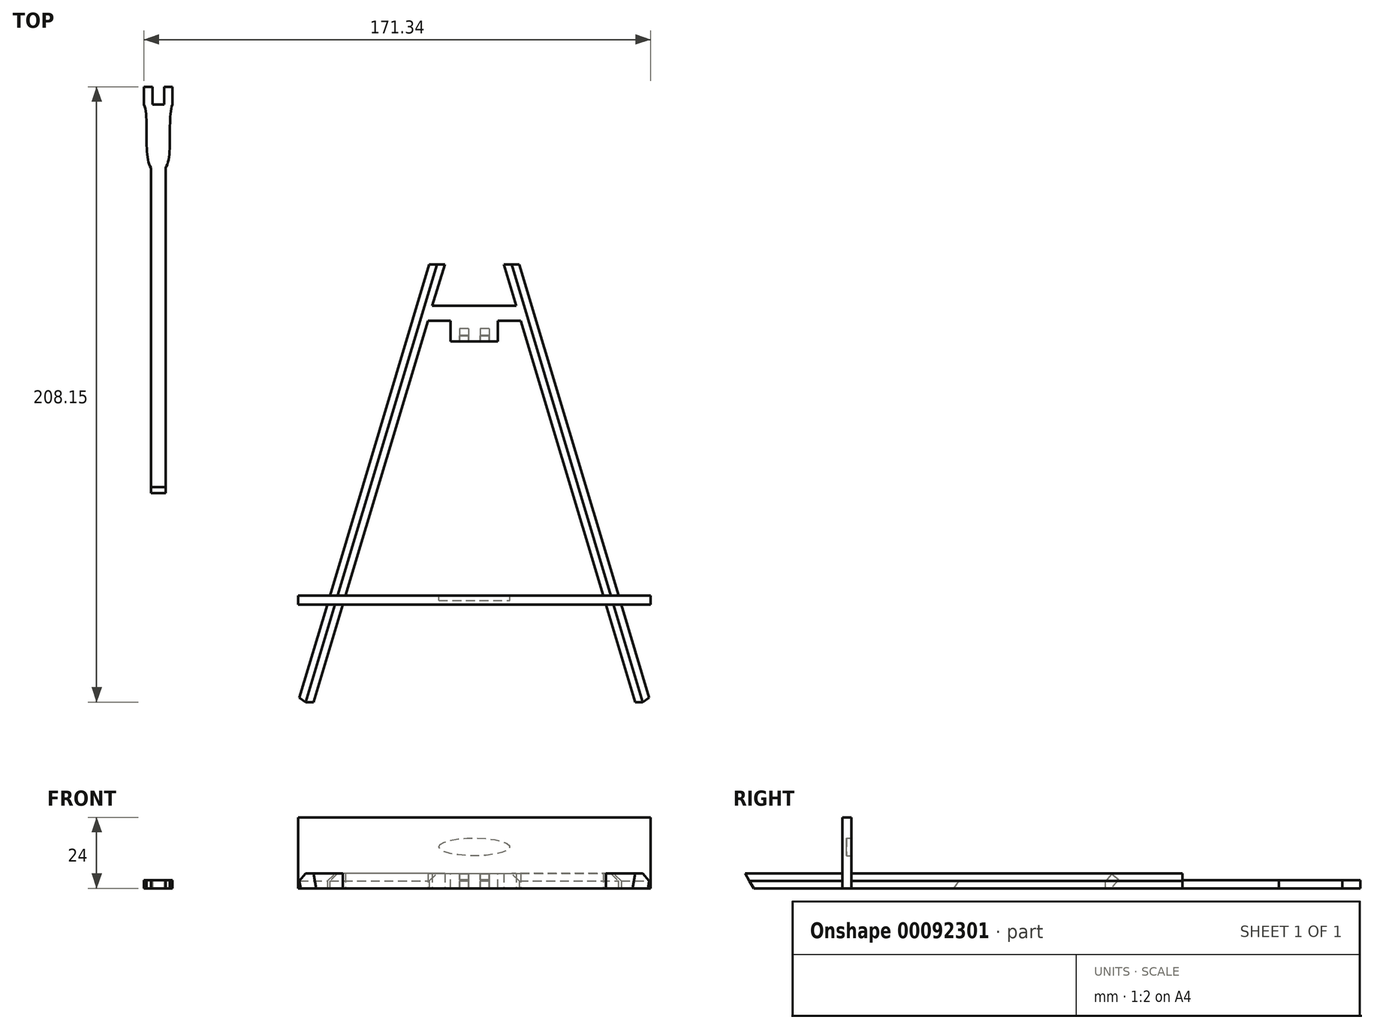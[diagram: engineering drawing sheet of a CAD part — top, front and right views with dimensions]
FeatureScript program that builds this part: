
annotation { "Feature Type Name" : "Feature", "Feature Type Description" : "" }
export const myFeature = defineFeature(function(context is Context, id is Id, definition is map)
    precondition{}
    {
        {
            var Q0;
            Q0=qCreatedBy(makeId("Top.planeOp"),FACE);
            var sketch = newSketch(context, id + "F0", { "sketchPlane" : qUnion([Q0])});
            skLineSegment(sketch, "E0.bottom", {"start": v(-52.21, 78.6) * mm, "end": v(57.79, 78.6) * mm});
            skLineSegment(sketch, "E0.top", {"start": v(-52.21, -71.4) * mm, "end": v(57.79, -71.4) * mm});
            skLineSegment(sketch, "E0.left", {"start": v(-52.21, 78.6) * mm, "end": v(-52.21, -71.4) * mm});
            skLineSegment(sketch, "E0.right", {"start": v(57.79, 78.6) * mm, "end": v(57.79, -71.4) * mm});
            skLineSegment(sketch, "E1", {"start": v(2.79, 78.6) * mm, "end": v(-7.21, 78.6) * mm});
            skLineSegment(sketch, "E2", {"start": v(2.79, 78.6) * mm, "end": v(12.79, 78.6) * mm});
            skLineSegment(sketch, "E3", {"start": v(-7.21, 78.6) * mm, "end": v(-52.21, -71.4) * mm});
            skLineSegment(sketch, "E4", {"start": v(12.79, 78.6) * mm, "end": v(57.79, -71.4) * mm});
            skLineSegment(sketch, "E5", {"start": v(-40.81, -33.4) * mm, "end": v(46.39, -33.4) * mm});
            skLineSegment(sketch, "E6.0", {"start": v(-12, 80.05) * mm, "end": v(-57, -69.95) * mm});
            skLineSegment(sketch, "E7.0", {"start": v(17.58, 80.05) * mm, "end": v(62.58, -69.95) * mm});
            skLineSegment(sketch, "E8.0", {"start": v(-41.71, -36.4) * mm, "end": v(47.29, -36.4) * mm});
            skLineSegment(sketch, "E9", {"start": v(-12, 80.05) * mm, "end": v(-7.21, 78.6) * mm});
            skLineSegment(sketch, "E10", {"start": v(12.79, 78.6) * mm, "end": v(17.58, 80.05) * mm});
            skLineSegment(sketch, "E11", {"start": v(-57, -69.95) * mm, "end": v(-52.21, -71.4) * mm});
            skLineSegment(sketch, "E12", {"start": v(57.79, -71.4) * mm, "end": v(62.58, -69.95) * mm});
            skLineSegment(sketch, "E13", {"start": v(-11.41, 64.6) * mm, "end": v(16.99, 64.6) * mm});
            skLineSegment(sketch, "E14.0", {"start": v(-12.91, 59.6) * mm, "end": v(18.49, 59.6) * mm});
            skLineSegment(sketch, "E15", {"start": v(2.79, 78.6) * mm, "end": v(2.79, 64.6) * mm, "construction": true});
            skLineSegment(sketch, "E16", {"start": v(2.79, -36.4) * mm, "end": v(2.79, -71.4) * mm, "construction": true});
            skSolve(sketch);
        }
        {
            var Q0;
            {var subQ0=sQuery(id+"F0.wireOp",EDGE,"E3");var subQ1=makeQuery(id+"F0.imprint","INTERSECT",VERTEX,{"derivedFrom":[subQ0,sQuery(id+"F0.wireOp",EDGE,"E13")]});Q0=makeQuery(id+"F0.imprint","IMPRINT",FACE,{"disambiguationData":[TD([[makeQuery(id+"F0.imprint","IMPRINT",EDGE,{"disambiguationData":[TD([[subQ1,-1.0]])],"derivedFrom":subQ0}),-1.0]])]});}
            var Q1;
            {var subQ0=sQuery(id+"F0.wireOp",EDGE,"E13");Q1=makeQuery(id+"F0.imprint","IMPRINT",FACE,{"disambiguationData":[TD([[makeQuery(id+"F0.imprint","IMPRINT",EDGE,{"derivedFrom":subQ0}),-1.0]])]});}
            var Q2;
            {var subQ0=sQuery(id+"F0.wireOp",EDGE,"E4");var subQ5=makeQuery(id+"F0.imprint","INTERSECT",VERTEX,{"derivedFrom":[subQ0,sQuery(id+"F0.wireOp",EDGE,"E13")]});Q2=makeQuery(id+"F0.imprint","IMPRINT",FACE,{"disambiguationData":[TD([[makeQuery(id+"F0.imprint","IMPRINT",EDGE,{"disambiguationData":[TD([[subQ5,-1.0]])],"derivedFrom":subQ0}),1.0]])]});}
            var Q3;
            {var subQ0=sQuery(id+"F0.wireOp",EDGE,"E5");Q3=makeQuery(id+"F0.imprint","IMPRINT",FACE,{"disambiguationData":[TD([[makeQuery(id+"F0.imprint","IMPRINT",EDGE,{"derivedFrom":subQ0}),-1.0]])]});}
            var Q4;
            {var subQ0=sQuery(id+"F0.wireOp",EDGE,"E11");Q4=makeQuery(id+"F0.imprint","IMPRINT",FACE,{"disambiguationData":[TD([[makeQuery(id+"F0.imprint","IMPRINT",EDGE,{"derivedFrom":subQ0}),1.0]])]});}
            var Q5;
            {var subQ0=sQuery(id+"F0.wireOp",EDGE,"E12");Q5=makeQuery(id+"F0.imprint","IMPRINT",FACE,{"disambiguationData":[TD([[makeQuery(id+"F0.imprint","IMPRINT",EDGE,{"derivedFrom":subQ0}),1.0]])]});}
            extrude(context, id + "F1", {"entities" : qUnion([Q0, Q1, Q2, Q3, Q4, Q5]), "depth" : 5 * mm});
        }
        {
            var Q0;
            Q0=makeQuery(id+"F1.opExtrude","CAP_FACE",FACE,{"disambiguationData":[OSD([sQuery(id+"F0.wireOp",EDGE,"E0.bottom"),sQuery(id+"F0.wireOp",EDGE,"E3"),sQuery(id+"F0.wireOp",EDGE,"E4"),sQuery(id+"F0.wireOp",EDGE,"E5"),sQuery(id+"F0.wireOp",EDGE,"E6.0"),sQuery(id+"F0.wireOp",EDGE,"E7.0"),sQuery(id+"F0.wireOp",EDGE,"E8.0"),sQuery(id+"F0.wireOp",EDGE,"E11"),sQuery(id+"F0.wireOp",EDGE,"E12"),sQuery(id+"F0.wireOp",EDGE,"E13"),sQuery(id+"F0.wireOp",EDGE,"E14.0")])],"isStart":true});
            var sketch = newSketch(context, id + "F2", { "sketchPlane" : qUnion([Q0])});
            skLineSegment(sketch, "E17.0", {"start": v(-40.81, 33.4) * mm, "end": v(46.39, 33.4) * mm});
            skLineSegment(sketch, "E18.0", {"start": v(-41.71, 36.4) * mm, "end": v(47.29, 36.4) * mm});
            skLineSegment(sketch, "E19", {"start": v(2.79, 3.1) * mm, "end": v(2.79, -57.6) * mm, "construction": true});
            skLineSegment(sketch, "E20", {"start": v(-41.71, 36.4) * mm, "end": v(-56.81, 36.4) * mm});
            skLineSegment(sketch, "E21", {"start": v(-56.81, 33.4) * mm, "end": v(-56.81, 36.4) * mm});
            skLineSegment(sketch, "E22", {"start": v(-56.81, 33.4) * mm, "end": v(-40.81, 33.4) * mm});
            skLineSegment(sketch, "E23.MirrorCS", {"start": v(47.29, 36.4) * mm, "end": v(62.39, 36.4) * mm});
            skLineSegment(sketch, "E24.MirrorCS", {"start": v(62.39, 33.4) * mm, "end": v(62.39, 36.4) * mm});
            skLineSegment(sketch, "E25.MirrorCS", {"start": v(62.39, 33.4) * mm, "end": v(46.39, 33.4) * mm});
            skSolve(sketch);
        }
        {
            var Q0;
            Q0 = qSketchRegion(id + "F2", true);
            extrude(context, id + "F3", {"entities" : qUnion([Q0]), "operationType" : NewBodyOperationType.ADD, "oppositeDirection" : true, "depth" : 24 * mm});
        }
        {
            var Q0;
            Q0=makeQuery(id+"F1.opExtrude","SWEPT_FACE",FACE,{"disambiguationData":[OSD([sQuery(id+"F0.wireOp",EDGE,"E14.0")])]});
            var sketch = newSketch(context, id + "F4", { "sketchPlane" : qUnion([Q0])});
            skLineSegment(sketch, "E26.bottom", {"start": v(10.79, 0) * mm, "end": v(-5.21, 0) * mm});
            skLineSegment(sketch, "E26.top", {"start": v(10.79, 5) * mm, "end": v(-5.21, 5) * mm});
            skLineSegment(sketch, "E26.left", {"start": v(10.79, 0) * mm, "end": v(10.79, 5) * mm});
            skLineSegment(sketch, "E26.right", {"start": v(-5.21, 0) * mm, "end": v(-5.21, 5) * mm});
            skLineSegment(sketch, "E27", {"start": v(2.79, 0) * mm, "end": v(2.79, 5) * mm, "construction": true});
            skSolve(sketch);
        }
        {
            var Q0;
            Q0 = qSketchRegion(id + "F4", true);
            extrude(context, id + "F5", {"entities" : qUnion([Q0]), "operationType" : NewBodyOperationType.ADD, "depth" : 7 * mm});
        }
        {
            var Q0;
            Q0=makeQuery(id+"F5.opExtrude","CAP_EDGE",EDGE,{"disambiguationData":[OSD([sQuery(id+"F4.wireOp",EDGE,"E26.bottom")])],"isStart":false});
            cPlane(context, id + "F6", {"entities" : qUnion([Q0]), "cplaneType" : CPlaneType.LINE_ANGLE, "offset" : 4 * mm, "angle" : 50 * degree, "width" : 150 * mm, "height" : 150 * mm});
        }
        {
            var Q0;
            Q0=qCreatedBy(id+"F6.planeOp",FACE);
            var sketch = newSketch(context, id + "F7", { "sketchPlane" : qUnion([Q0])});
            skLineSegment(sketch, "E28.bottom", {"start": v(-0.79, -27.8) * mm, "end": v(2.21, -27.8) * mm});
            skLineSegment(sketch, "E28.top", {"start": v(-0.79, -24.8) * mm, "end": v(2.21, -24.8) * mm});
            skLineSegment(sketch, "E28.left", {"start": v(-0.79, -27.8) * mm, "end": v(-0.79, -24.8) * mm});
            skPoint(sketch, "E29.0", {"position": v(10.79, 40.3) * mm});
            skPoint(sketch, "E29.1", {"position": v(-5.21, 40.3) * mm});
            skLineSegment(sketch, "E30.bottom", {"start": v(7.79, 41.8) * mm, "end": v(4.79, 41.8) * mm});
            skLineSegment(sketch, "E30.top", {"start": v(7.79, 38.8) * mm, "end": v(4.79, 38.8) * mm});
            skLineSegment(sketch, "E30.left", {"start": v(7.79, 41.8) * mm, "end": v(7.79, 38.8) * mm});
            skLineSegment(sketch, "E30.right", {"start": v(4.79, 41.8) * mm, "end": v(4.79, 38.8) * mm});
            skLineSegment(sketch, "E31", {"start": v(10.79, 40.3) * mm, "end": v(7.79, 40.3) * mm, "construction": true});
            skLineSegment(sketch, "E32", {"start": v(10.79, 40.3) * mm, "end": v(-5.21, 40.3) * mm, "construction": true});
            skLineSegment(sketch, "E33.bottom", {"start": v(0.79, 41.8) * mm, "end": v(-2.21, 41.8) * mm});
            skLineSegment(sketch, "E33.top", {"start": v(0.79, 38.8) * mm, "end": v(-2.21, 38.8) * mm});
            skLineSegment(sketch, "E33.left", {"start": v(0.79, 41.8) * mm, "end": v(0.79, 38.8) * mm});
            skLineSegment(sketch, "E33.right", {"start": v(-2.21, 41.8) * mm, "end": v(-2.21, 38.8) * mm});
            skLineSegment(sketch, "E34", {"start": v(-5.21, 40.3) * mm, "end": v(-2.21, 40.3) * mm, "construction": true});
            skSolve(sketch);
        }
        {
            var Q0;
            Q0 = qSketchRegion(id + "F7", true);
            extrude(context, id + "F8", {"entities" : qUnion([Q0]), "operationType" : NewBodyOperationType.REMOVE, "depth" : 5 * mm});
        }
        {
            var Q0;
            Q0=qCreatedBy(makeId("Top.planeOp"),FACE);
            var sketch = newSketch(context, id + "F9", { "sketchPlane" : qUnion([Q0])});
            skLineSegment(sketch, "E35.bottom", {"start": v(-101.65, 1.29) * mm, "end": v(-106.65, 1.29) * mm});
            skLineSegment(sketch, "E35.top", {"start": v(-101.65, 111.29) * mm, "end": v(-106.65, 111.29) * mm});
            skLineSegment(sketch, "E35.left", {"start": v(-101.65, 1.29) * mm, "end": v(-101.65, 111.29) * mm});
            skLineSegment(sketch, "E35.right", {"start": v(-106.65, 1.29) * mm, "end": v(-106.65, 111.29) * mm});
            skPoint(sketch, "E35.middle", {"position": v(-104.15, 56.29) * mm});
            skLineSegment(sketch, "E36.bottom", {"start": v(-99.35, 138.76) * mm, "end": v(-102.15, 138.76) * mm});
            skLineSegment(sketch, "E36.top", {"start": v(-99.35, 132.76) * mm, "end": v(-102.15, 132.76) * mm});
            skLineSegment(sketch, "E36.left", {"start": v(-99.35, 138.76) * mm, "end": v(-99.35, 132.76) * mm});
            skLineSegment(sketch, "E36.right", {"start": v(-102.15, 138.76) * mm, "end": v(-102.15, 132.76) * mm});
            skLineSegment(sketch, "E37.bottom", {"start": v(-106.15, 138.76) * mm, "end": v(-108.95, 138.76) * mm});
            skLineSegment(sketch, "E37.top", {"start": v(-106.15, 132.76) * mm, "end": v(-108.95, 132.76) * mm});
            skLineSegment(sketch, "E37.left", {"start": v(-106.15, 138.76) * mm, "end": v(-106.15, 132.76) * mm});
            skLineSegment(sketch, "E37.right", {"start": v(-108.95, 138.76) * mm, "end": v(-108.95, 132.76) * mm});
            skLineSegment(sketch, "E38", {"start": v(-101.65, 111.29) * mm, "end": v(-101.65, 132.76) * mm, "construction": true});
            skLineSegment(sketch, "E39", {"start": v(-106.65, 111.29) * mm, "end": v(-106.65, 132.76) * mm, "construction": true});
            skLineSegment(sketch, "E40", {"start": v(-101.65, 132.76) * mm, "end": v(-106.65, 132.76) * mm, "construction": true});
            skLineSegment(sketch, "E41", {"start": v(-102.15, 132.76) * mm, "end": v(-101.65, 132.76) * mm, "construction": true});
            skLineSegment(sketch, "E42", {"start": v(-106.15, 132.76) * mm, "end": v(-106.65, 132.76) * mm, "construction": true});
            skFitSpline(sketch, "E43", {"points": [v(-99.35, 132.76) * mm, v(-101.65, 111.29) * mm, v(-106.65, 111.29) * mm, v(-108.95, 132.76) * mm], "startDerivative": vector(-13.95, -37.86) * mm, "endDerivative": vector(-13.95, 37.86) * mm});
            skLineSegment(sketch, "E44", {"start": v(-102.15, 132.76) * mm, "end": v(-106.15, 132.76) * mm});
            skSolve(sketch);
        }
        {
            var Q0;
            Q0=makeQuery(id+"F9.imprint","IMPRINT",FACE,{"disambiguationData":[TD([[makeQuery(id+"F9.imprint","IMPRINT",EDGE,{"derivedFrom":sQuery(id+"F9.wireOp",EDGE,"E35.bottom")}),-1.0]])]});
            var Q1;
            {var subQ1=sQuery(id+"F9.wireOp",EDGE,"E35.top");Q1=makeQuery(id+"F9.imprint","IMPRINT",FACE,{"disambiguationData":[TD([[makeQuery(id+"F9.imprint","IMPRINT",EDGE,{"derivedFrom":subQ1}),-1.0]])]});}
            var Q2;
            Q2=makeQuery(id+"F9.imprint","IMPRINT",FACE,{"disambiguationData":[TD([[makeQuery(id+"F9.imprint","IMPRINT",EDGE,{"derivedFrom":sQuery(id+"F9.wireOp",EDGE,"E36.bottom")}),1.0]])]});
            var Q3;
            Q3=makeQuery(id+"F9.imprint","IMPRINT",FACE,{"disambiguationData":[TD([[makeQuery(id+"F9.imprint","IMPRINT",EDGE,{"derivedFrom":sQuery(id+"F9.wireOp",EDGE,"E37.bottom")}),1.0]])]});
            var Q4;
            {var subQ0=sQuery(id+"F9.wireOp",EDGE,"E35.top");Q4=makeQuery(id+"F9.imprint","IMPRINT",FACE,{"disambiguationData":[TD([[makeQuery(id+"F9.imprint","IMPRINT",EDGE,{"derivedFrom":subQ0}),1.0]])]});}
            extrude(context, id + "F10", {"entities" : qUnion([Q0, Q1, Q2, Q3, Q4]), "depth" : 2.8 * mm});
        }
        {
            var Q0;
            Q0=makeQuery(id+"F10.opExtrude","CAP_EDGE",EDGE,{"disambiguationData":[OSD([sQuery(id+"F9.wireOp",EDGE,"E35.bottom")])],"isStart":false});
            chamfer(context, id + "F11", {"entities" : qUnion([Q0]), "chamferType" : ChamferType.TWO_OFFSETS, "width1" : 2.8 * mm, "oppositeDirection" : false, "width2" : 2 * mm, "tangentPropagation" : true});
        }
        {
            var Q0;
            Q0=makeQuery(id+"F1.opExtrude","CAP_VERTEX",VERTEX,{"disambiguationData":[OSD([sQuery(id+"F0.wireOp",EDGE,"E0.top"),sQuery(id+"F0.wireOp",EDGE,"E0.left"),sQuery(id+"F0.wireOp",EDGE,"E3"),sQuery(id+"F0.wireOp",EDGE,"E11")])],"isStart":false});
            var Q1;
            Q1=makeQuery(id+"F1.opExtrude","CAP_VERTEX",VERTEX,{"disambiguationData":[OSD([sQuery(id+"F0.wireOp",EDGE,"E0.top"),sQuery(id+"F0.wireOp",EDGE,"E0.right"),sQuery(id+"F0.wireOp",EDGE,"E4"),sQuery(id+"F0.wireOp",EDGE,"E12")])],"isStart":false});
            var Q2;
            Q2=makeQuery(id+"F1.opExtrude","CAP_VERTEX",VERTEX,{"disambiguationData":[OSD([sQuery(id+"F0.wireOp",EDGE,"E0.top"),sQuery(id+"F0.wireOp",EDGE,"E0.right"),sQuery(id+"F0.wireOp",EDGE,"E4"),sQuery(id+"F0.wireOp",EDGE,"E12")])],"isStart":true});
            cPlane(context, id + "F12", {"entities" : qUnion([Q0, Q1, Q2]), "cplaneType" : CPlaneType.THREE_POINT, "offset" : 150 * mm, "width" : 150 * mm, "height" : 150 * mm});
        }
        {
            var Q0;
            Q0=qCreatedBy(id+"F12.planeOp",FACE);
            var sketch = newSketch(context, id + "F13", { "sketchPlane" : qUnion([Q0])});
            skLineSegment(sketch, "E45.bottom", {"start": v(-65.92, 12.39) * mm, "end": v(74.93, 12.39) * mm});
            skLineSegment(sketch, "E45.top", {"start": v(-65.92, -10.23) * mm, "end": v(74.93, -10.23) * mm});
            skLineSegment(sketch, "E45.left", {"start": v(-65.92, 12.39) * mm, "end": v(-65.92, -10.23) * mm});
            skLineSegment(sketch, "E45.right", {"start": v(74.93, 12.39) * mm, "end": v(74.93, -10.23) * mm});
            skSolve(sketch);
        }
        {
            var Q0;
            Q0 = qSketchRegion(id + "F13", true);
            extrude(context, id + "F14", {"entities" : qUnion([Q0]), "operationType" : NewBodyOperationType.REMOVE, "oppositeDirection" : true, "depth" : 2 * mm});
        }
        {
            var Q0;
            {var subQ0=sQuery(id+"F0.wireOp",EDGE,"E8.0");var subQ2=sQuery(id+"F0.wireOp",EDGE,"E14.0");var subQ3=sQuery(id+"F0.wireOp",EDGE,"E13");var subQ4=sQuery(id+"F0.wireOp",EDGE,"E12");var subQ5=sQuery(id+"F0.wireOp",EDGE,"E11");var subQ6=sQuery(id+"F0.wireOp",EDGE,"E7.0");var subQ7=sQuery(id+"F0.wireOp",EDGE,"E6.0");var subQ8=sQuery(id+"F0.wireOp",EDGE,"E5");var subQ9=sQuery(id+"F0.wireOp",EDGE,"E4");var subQ10=sQuery(id+"F0.wireOp",EDGE,"E3");var subQ11=sQuery(id+"F0.wireOp",EDGE,"E0.bottom");var subQ14=sQuery(id+"F2.wireOp",EDGE,"E25.MirrorCS");var subQ15=sQuery(id+"F2.wireOp",EDGE,"E22");var subQ16=sQuery(id+"F2.wireOp",EDGE,"E17.0");var subQ18=sQuery(id+"F2.wireOp",EDGE,"E23.MirrorCS");var subQ19=sQuery(id+"F2.wireOp",EDGE,"E20");var subQ20=sQuery(id+"F2.wireOp",EDGE,"E18.0");var subQ22=sQuery(id+"F2.wireOp",EDGE,"E24.MirrorCS");var subQ23=sQuery(id+"F2.wireOp",EDGE,"E21");var subQ24=makeQuery(id+"F3.opExtrude","CAP_FACE",FACE,{"disambiguationData":[OSD([subQ16,subQ20,subQ19,subQ23,subQ15,subQ18,subQ22,subQ14])],"isStart":true});Q0=makeQuery(id+"F14.boolean.opBoolean","INTERSECT",EDGE,{"disambiguationData":[OD(1.0)],"derivedFrom":[makeQuery(id+"FEiG26peZH11kR7_2.boolean.opBoolean","MERGE",FACE,{"derivedFrom":[makeQuery(id+"F5.boolean.opBoolean","MERGE",FACE,{"derivedFrom":[makeQuery(id+"F1.opExtrude","CAP_FACE",FACE,{"disambiguationData":[OSD([subQ11,subQ10,subQ9,subQ8,subQ7,subQ6,subQ0,subQ5,subQ4,subQ3,subQ2])],"isStart":true}),makeQuery(id+"F5.opExtrude","SWEPT_FACE",FACE,{"disambiguationData":[OSD([sQuery(id+"F4.wireOp",EDGE,"E26.bottom")])]})]}),makeQuery(id+"FEiG26peZH11kR7_2.opExtrude","CAP_FACE",FACE,{"disambiguationData":[OSD([subQ16,subQ20,subQ19,subQ23,subQ15,subQ18,subQ22,subQ14]),TDD([makeQuery(id+"F3.boolean.opBoolean","SPLIT",FACE,{"disambiguationData":[TD([makeQuery(id+"F1.opExtrude","SWEPT_FACE",FACE,{"disambiguationData":[OSD([subQ7])]})])],"derivedFrom":subQ24})])],"isStart":false}),makeQuery(id+"FEiG26peZH11kR7_2.opExtrude","CAP_FACE",FACE,{"disambiguationData":[OSD([subQ16,subQ20,subQ19,subQ23,subQ15,subQ18,subQ22,subQ14]),TDD([makeQuery(id+"F3.boolean.opBoolean","SPLIT",FACE,{"disambiguationData":[TD([makeQuery(id+"F1.opExtrude","SWEPT_FACE",FACE,{"disambiguationData":[OSD([subQ6])]})])],"derivedFrom":subQ24})])],"isStart":false})]}),makeQuery(id+"F14.opExtrude","CAP_FACE",FACE,{"disambiguationData":[OSD([sQuery(id+"F13.wireOp",EDGE,"E45.bottom"),sQuery(id+"F13.wireOp",EDGE,"E45.top"),sQuery(id+"F13.wireOp",EDGE,"E45.left"),sQuery(id+"F13.wireOp",EDGE,"E45.right")])],"isStart":false})]});}
            var Q1;
            {var subQ0=sQuery(id+"F0.wireOp",EDGE,"E8.0");var subQ2=sQuery(id+"F0.wireOp",EDGE,"E14.0");var subQ3=sQuery(id+"F0.wireOp",EDGE,"E13");var subQ4=sQuery(id+"F0.wireOp",EDGE,"E12");var subQ5=sQuery(id+"F0.wireOp",EDGE,"E11");var subQ6=sQuery(id+"F0.wireOp",EDGE,"E7.0");var subQ7=sQuery(id+"F0.wireOp",EDGE,"E6.0");var subQ8=sQuery(id+"F0.wireOp",EDGE,"E5");var subQ9=sQuery(id+"F0.wireOp",EDGE,"E4");var subQ10=sQuery(id+"F0.wireOp",EDGE,"E3");var subQ11=sQuery(id+"F0.wireOp",EDGE,"E0.bottom");var subQ14=sQuery(id+"F2.wireOp",EDGE,"E25.MirrorCS");var subQ15=sQuery(id+"F2.wireOp",EDGE,"E22");var subQ16=sQuery(id+"F2.wireOp",EDGE,"E17.0");var subQ18=sQuery(id+"F2.wireOp",EDGE,"E23.MirrorCS");var subQ19=sQuery(id+"F2.wireOp",EDGE,"E20");var subQ20=sQuery(id+"F2.wireOp",EDGE,"E18.0");var subQ22=sQuery(id+"F2.wireOp",EDGE,"E24.MirrorCS");var subQ23=sQuery(id+"F2.wireOp",EDGE,"E21");var subQ24=makeQuery(id+"F3.opExtrude","CAP_FACE",FACE,{"disambiguationData":[OSD([subQ16,subQ20,subQ19,subQ23,subQ15,subQ18,subQ22,subQ14])],"isStart":true});Q1=makeQuery(id+"F14.boolean.opBoolean","INTERSECT",EDGE,{"disambiguationData":[OD(0.0)],"derivedFrom":[makeQuery(id+"FEiG26peZH11kR7_2.boolean.opBoolean","MERGE",FACE,{"derivedFrom":[makeQuery(id+"F5.boolean.opBoolean","MERGE",FACE,{"derivedFrom":[makeQuery(id+"F1.opExtrude","CAP_FACE",FACE,{"disambiguationData":[OSD([subQ11,subQ10,subQ9,subQ8,subQ7,subQ6,subQ0,subQ5,subQ4,subQ3,subQ2])],"isStart":true}),makeQuery(id+"F5.opExtrude","SWEPT_FACE",FACE,{"disambiguationData":[OSD([sQuery(id+"F4.wireOp",EDGE,"E26.bottom")])]})]}),makeQuery(id+"FEiG26peZH11kR7_2.opExtrude","CAP_FACE",FACE,{"disambiguationData":[OSD([subQ16,subQ20,subQ19,subQ23,subQ15,subQ18,subQ22,subQ14]),TDD([makeQuery(id+"F3.boolean.opBoolean","SPLIT",FACE,{"disambiguationData":[TD([makeQuery(id+"F1.opExtrude","SWEPT_FACE",FACE,{"disambiguationData":[OSD([subQ7])]})])],"derivedFrom":subQ24})])],"isStart":false}),makeQuery(id+"FEiG26peZH11kR7_2.opExtrude","CAP_FACE",FACE,{"disambiguationData":[OSD([subQ16,subQ20,subQ19,subQ23,subQ15,subQ18,subQ22,subQ14]),TDD([makeQuery(id+"F3.boolean.opBoolean","SPLIT",FACE,{"disambiguationData":[TD([makeQuery(id+"F1.opExtrude","SWEPT_FACE",FACE,{"disambiguationData":[OSD([subQ6])]})])],"derivedFrom":subQ24})])],"isStart":false})]}),makeQuery(id+"F14.opExtrude","CAP_FACE",FACE,{"disambiguationData":[OSD([sQuery(id+"F13.wireOp",EDGE,"E45.bottom"),sQuery(id+"F13.wireOp",EDGE,"E45.top"),sQuery(id+"F13.wireOp",EDGE,"E45.left"),sQuery(id+"F13.wireOp",EDGE,"E45.right")])],"isStart":false})]});}
            chamfer(context, id + "F15", {"entities" : qUnion([Q0, Q1]), "chamferType" : ChamferType.TWO_OFFSETS, "width1" : 5 * mm, "oppositeDirection" : false, "width2" : 3 * mm, "tangentPropagation" : true});
        }
        {
            var Q0;
            Q0=makeQuery(id+"F3.boolean.opBoolean","MERGE",FACE,{"derivedFrom":[makeQuery(id+"F1.opExtrude","SWEPT_FACE",FACE,{"disambiguationData":[OSD([sQuery(id+"F0.wireOp",EDGE,"E5")])]}),makeQuery(id+"F3.opExtrude","SWEPT_FACE",FACE,{"disambiguationData":[OSD([sQuery(id+"F2.wireOp",EDGE,"E17.0"),sQuery(id+"F2.wireOp",EDGE,"E22"),sQuery(id+"F2.wireOp",EDGE,"E25.MirrorCS")])]})]});
            var sketch = newSketch(context, id + "F16", { "sketchPlane" : qUnion([Q0])});
            skLineSegment(sketch, "E46.0", {"start": v(40.81, 0) * mm, "end": v(-46.39, 0) * mm, "construction": true});
            skLineSegment(sketch, "E47", {"start": v(-2.79, 0) * mm, "end": v(-2.79, 14) * mm, "construction": true});
            skEllipse(sketch, "E48", {"center": v(-2.79, 14) * mm, "majorRadius": 12 * mm, "minorRadius": 3 * mm, "majorAxis": v(1, 0)});
            skSolve(sketch);
        }
        {
            var Q0;
            Q0=makeQuery(id+"F16.imprint","IMPRINT",FACE,{"disambiguationData":[TD([[makeQuery(id+"F16.imprint","IMPRINT",EDGE,{"derivedFrom":sQuery(id+"F16.wireOp",EDGE,"E48")}),1.0]])]});
            extrude(context, id + "F17", {"entities" : qUnion([Q0]), "operationType" : NewBodyOperationType.REMOVE, "oppositeDirection" : true, "depth" : 1.6 * mm});
        }
        {
            var Q0;
            {var subQ0=sQuery(id+"F0.wireOp",EDGE,"E6.0");var subQ1=sQuery(id+"F0.wireOp",EDGE,"E5");Q0=makeQuery(id+"F3.boolean.opBoolean","SPLIT",EDGE,{"disambiguationData":[TD([makeQuery(id+"F1.opExtrude","SWEPT_FACE",FACE,{"disambiguationData":[OSD([subQ1])]})])],"derivedFrom":makeQuery(id+"F1.opExtrude","CAP_EDGE",EDGE,{"disambiguationData":[OSD([subQ0])],"isStart":false})});}
            var Q1;
            {var subQ0=sQuery(id+"F0.wireOp",EDGE,"E7.0");var subQ1=sQuery(id+"F0.wireOp",EDGE,"E5");Q1=makeQuery(id+"F3.boolean.opBoolean","SPLIT",EDGE,{"disambiguationData":[TD([makeQuery(id+"F1.opExtrude","SWEPT_FACE",FACE,{"disambiguationData":[OSD([subQ1])]})])],"derivedFrom":makeQuery(id+"F1.opExtrude","CAP_EDGE",EDGE,{"disambiguationData":[OSD([subQ0])],"isStart":false})});}
            var Q2;
            {var subQ1=sQuery(id+"F0.wireOp",EDGE,"E8.0");var subQ2=sQuery(id+"F0.wireOp",EDGE,"E6.0");Q2=makeQuery(id+"F3.boolean.opBoolean","SPLIT",EDGE,{"disambiguationData":[TD([makeQuery(id+"F1.opExtrude","SWEPT_FACE",FACE,{"disambiguationData":[OSD([subQ1])]})])],"derivedFrom":makeQuery(id+"F1.opExtrude","CAP_EDGE",EDGE,{"disambiguationData":[OSD([subQ2])],"isStart":false})});}
            var Q3;
            {var subQ1=sQuery(id+"F0.wireOp",EDGE,"E8.0");var subQ2=sQuery(id+"F0.wireOp",EDGE,"E7.0");Q3=makeQuery(id+"F3.boolean.opBoolean","SPLIT",EDGE,{"disambiguationData":[TD([makeQuery(id+"F1.opExtrude","SWEPT_FACE",FACE,{"disambiguationData":[OSD([subQ1])]})])],"derivedFrom":makeQuery(id+"F1.opExtrude","CAP_EDGE",EDGE,{"disambiguationData":[OSD([subQ2])],"isStart":false})});}
            chamfer(context, id + "F18", {"entities" : qUnion([Q0, Q1, Q2, Q3]), "width" : 2.5 * mm, "tangentPropagation" : true});
        }
    });
